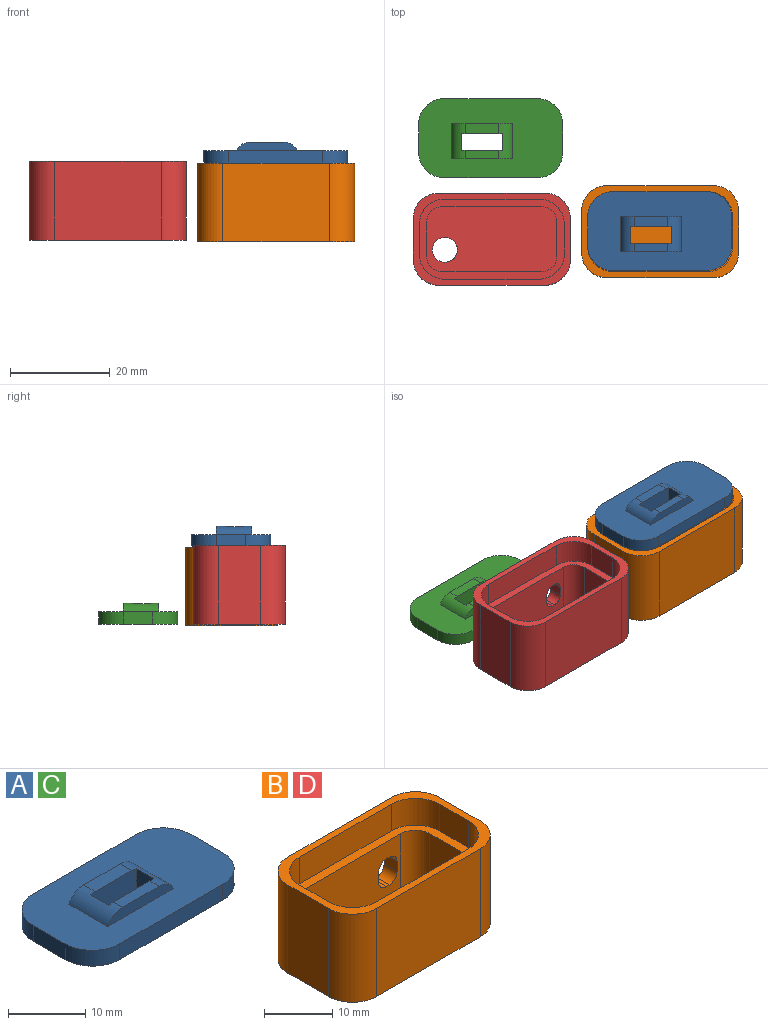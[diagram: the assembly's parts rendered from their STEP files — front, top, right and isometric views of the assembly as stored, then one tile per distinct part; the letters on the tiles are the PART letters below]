
ASSEMBLY  parts=4 mates=1
PART A: 20 faces, bbox 28.8x15.8x4.2 mm
  f0: plane 6.69x2.1mm, normal (0,0,1), area 14.1mm2, adj f7,f10,f18,f19
  f1: plane 28.8x15.8mm, normal (0,0,-1), area 406.2mm2, adj f3,f4,f5,f6,f9,f10,f11,f12
  f2: plane 28.8x15.8mm, normal (0,0,1), area 347.7mm2, adj f3,f4,f5,f6,f7,f8,f14,f15
  f3: plane 18.8x2.5mm, normal (0,1,0), area 47mm2, adj f1,f2,f14,f17
  f4: plane 5.8x2.5mm, normal (-1,0,0), area 14.5mm2, adj f1,f2,f14,f15
  f5: plane 18.8x2.5mm, normal (0,-1,0), area 47mm2, adj f1,f2,f15,f16
  f6: plane 5.8x2.5mm, normal (1,0,0), area 14.5mm2, adj f1,f2,f16,f17
  f7: plane 12.1x1.7mm, normal (0,1,0), area 18mm2, adj f0,f2,f18,f19
  f8: plane 12.1x1.7mm, normal (0,-1,0), area 18mm2, adj f2,f13,f18,f19
  f9: plane 4.09x3.3mm, normal (1,0,0), area 13.5mm2, adj f1,f10,f12,f18
  f10: plane 8.3x4.2mm, normal (0,-1,0), area 34.8mm2, adj f0,f1,f9,f11,f18,f19
  f11: plane 4.09x3.3mm, normal (-1,0,0), area 13.5mm2, adj f1,f10,f12,f19
  f12: plane 8.3x4.2mm, normal (0,1,0), area 34.8mm2, adj f1,f9,f11,f13,f18,f19
  f13: plane 6.69x1.7mm, normal (0,0,1), area 11.4mm2, adj f8,f12,f18,f19
  f14: cylinder r=5mm len=5mm, axis (0,0,1), area 19.6mm2, adj f1,f2,f3,f4
  f15: cylinder r=5mm len=5mm, axis (0,0,-1), area 19.6mm2, adj f1,f2,f4,f5
  f16: cylinder r=5mm len=5mm, axis (0,0,1), area 19.6mm2, adj f1,f2,f5,f6
  f17: cylinder r=5mm len=5mm, axis (0,0,-1), area 19.6mm2, adj f1,f2,f3,f6
  f18: cylinder r=3mm len=7.1mm, axis (0,-1,0), area 21.2mm2, adj f0,f2,f7,f8,f9,f10,f12,f13
  f19: cylinder r=3mm len=7.1mm, axis (0,-1,0), area 21.2mm2, adj f0,f2,f7,f8,f10,f11,f12,f13
PART B: 37 faces, bbox 31.4x18.4x15.8 mm
  f0: plane 21.4x15.8mm, normal (0,1,0), area 321.3mm2, adj f3,f7,f17,f18,f25,f26,f27,f28
  f1: plane 20x10mm, normal (0,-1,0), area 183.2mm2, adj f2,f23,f25,f26,f27,f28,f29,f30
  f2: plane 29x16mm, normal (0,0,1), area 112.3mm2, adj f1,f8,f9,f10,f11,f12,f13,f14
  f3: plane 31.4x18.4mm, normal (0,0,1), area 113.8mm2, adj f0,f4,f5,f6,f8,f9,f10,f11
  f4: plane 21.4x15.8mm, normal (0,-1,0), area 338.1mm2, adj f3,f7,f16,f19
  f5: plane 15.8x8.4mm, normal (1,0,0), area 132.7mm2, adj f3,f7,f16,f17
  f6: plane 15.8x8.4mm, normal (-1,0,0), area 132.7mm2, adj f3,f7,f18,f19
  f7: plane 31.4x18.4mm, normal (0,0,-1), area 536.7mm2, adj f0,f4,f5,f6,f16,f17,f18,f19
  f8: plane 19x4.8mm, normal (0,-1,0), area 91.2mm2, adj f2,f3,f12,f15
  f9: plane 6x4.8mm, normal (1,0,0), area 28.8mm2, adj f2,f3,f12,f13
  f10: plane 19x4.8mm, normal (0,1,0), area 91.2mm2, adj f2,f3,f13,f14
  f11: plane 6x4.8mm, normal (-1,0,0), area 28.8mm2, adj f2,f3,f14,f15
  f12: cylinder r=5mm len=5mm, axis (0,0,1), area 37.7mm2, adj f2,f3,f8,f9
  f13: cylinder r=5mm len=5mm, axis (0,0,-1), area 37.7mm2, adj f2,f3,f9,f10
  f14: cylinder r=5mm len=5mm, axis (0,0,1), area 37.7mm2, adj f2,f3,f10,f11
  f15: cylinder r=5mm len=5mm, axis (0,0,-1), area 37.7mm2, adj f2,f3,f8,f11
  f16: cylinder r=5mm len=15.8mm, axis (0,0,1), area 124.1mm2, adj f3,f4,f5,f7
  f17: cylinder r=5mm len=15.8mm, axis (0,0,-1), area 124.1mm2, adj f0,f3,f5,f7
  f18: cylinder r=5mm len=15.8mm, axis (0,0,1), area 124.1mm2, adj f0,f3,f6,f7
  f19: cylinder r=5mm len=15.8mm, axis (0,0,-1), area 124.1mm2, adj f3,f4,f6,f7
  f20: plane 20x10mm, normal (0,1,0), area 200mm2, adj f2,f23,f33,f36
  f21: plane 10x7mm, normal (-1,0,0), area 70mm2, adj f2,f23,f33,f34
  f22: plane 10x7mm, normal (1,0,0), area 70mm2, adj f2,f23,f35,f36
  f23: plane 26x13mm, normal (0,0,1), area 310.6mm2, adj f1,f20,f21,f22,f24,f33,f34,f35
  f24: cylinder r=2.5mm len=5mm, axis (0,0,-1), area 15.7mm2, adj f7,f23
  f25: plane 2.7x0.6mm, normal (0,0,1), area 1.6mm2, adj f0,f1,f29,f32
  f26: plane 2.7x1.8mm, normal (1,0,0), area 4.9mm2, adj f0,f1,f29,f30
  f27: plane 2.7x0.6mm, normal (0,0,-1), area 1.6mm2, adj f0,f1,f30,f31
  f28: plane 2.7x1.8mm, normal (-1,0,0), area 4.9mm2, adj f0,f1,f31,f32
  f29: cylinder r=1.6mm len=2.7mm, axis (0,1,0), area 6.8mm2, adj f0,f1,f25,f26
  f30: cylinder r=1.6mm len=2.7mm, axis (0,-1,0), area 6.8mm2, adj f0,f1,f26,f27
  f31: cylinder r=1.6mm len=2.7mm, axis (0,1,0), area 6.8mm2, adj f0,f1,f27,f28
  f32: cylinder r=1.6mm len=2.7mm, axis (0,-1,0), area 6.8mm2, adj f0,f1,f25,f28
  f33: cylinder r=3mm len=10mm, axis (0,0,1), area 47.1mm2, adj f2,f20,f21,f23
  f34: cylinder r=3mm len=10mm, axis (0,0,-1), area 47.1mm2, adj f1,f2,f21,f23
  f35: cylinder r=3mm len=10mm, axis (0,0,1), area 47.1mm2, adj f1,f2,f22,f23
  f36: cylinder r=3mm len=10mm, axis (0,0,-1), area 47.1mm2, adj f2,f20,f22,f23
PART C: same geometry as A
PART D: same geometry as B
PLACE A t=(33.77,-23.5,15.98)mm
PLACE B t=(33.65,-3.38,0.18)mm
PLACE C t=(-0.01,-4.89,0.52)mm
PLACE D t=(-0.01,-4.89,0.52)mm
MATE revolute A.f14 <-> B.f12  axis (0,0,-1) through (24.15,-0.38,15.98)mm
